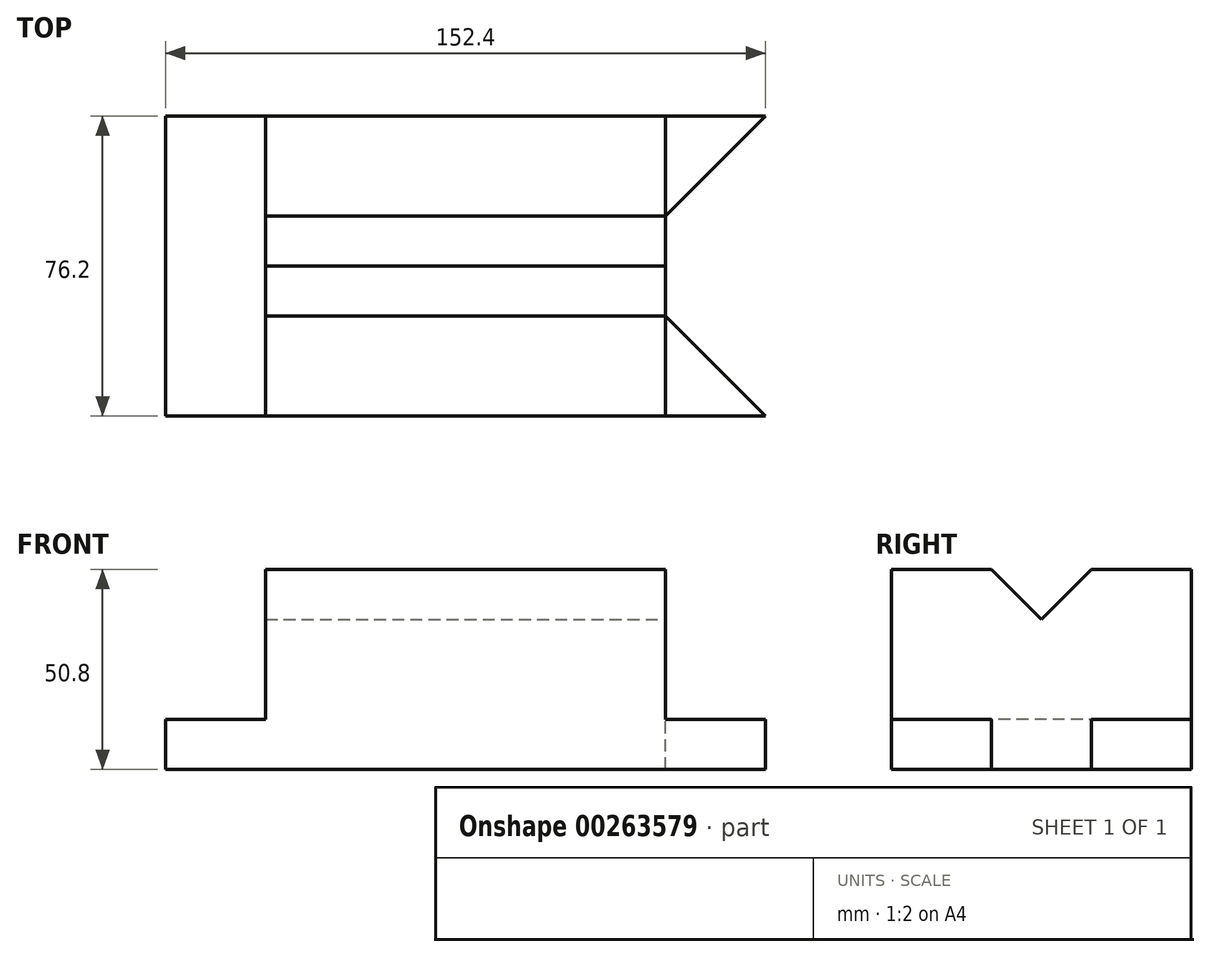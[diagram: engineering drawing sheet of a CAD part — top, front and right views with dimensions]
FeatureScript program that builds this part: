
annotation { "Feature Type Name" : "Feature", "Feature Type Description" : "" }
export const myFeature = defineFeature(function(context is Context, id is Id, definition is map)
    precondition{}
    {
        {
            var Q0;
            Q0=qCreatedBy(makeId("Front.planeOp"),FACE);
            var sketch = newSketch(context, id + "F0", { "sketchPlane" : qUnion([Q0])});
            skLineSegment(sketch, "E0.bottom", {"start": v(-85.05, 48.2) * mm, "end": v(67.35, 48.2) * mm});
            skLineSegment(sketch, "E0.top", {"start": v(-85.05, -2.6) * mm, "end": v(67.35, -2.6) * mm});
            skLineSegment(sketch, "E0.left", {"start": v(-85.05, 48.2) * mm, "end": v(-85.05, -2.6) * mm});
            skLineSegment(sketch, "E0.right", {"start": v(67.35, 48.2) * mm, "end": v(67.35, -2.6) * mm});
            skSolve(sketch);
        }
        {
            var Q0;
            Q0=makeQuery(id+"F0.imprint","IMPRINT",FACE,{"disambiguationData":[TD([[makeQuery(id+"F0.imprint","IMPRINT",EDGE,{"derivedFrom":sQuery(id+"F0.wireOp",EDGE,"E0.bottom")}),-1.0]])]});
            var sketch = newSketch(context, id + "F1", { "sketchPlane" : qUnion([Q0])});
            skSolve(sketch);
        }
        {
            var Q0;
            Q0 = qSketchRegion(id + "F1", true);
            var Q1;
            Q1=makeQuery(id+"F1.imprint","IMPRINT",FACE,{"disambiguationData":[TD([[makeQuery(id+"F1.imprint","IMPRINT",EDGE,{"derivedFrom":makeQuery(id+"F0.imprint","IMPRINT",EDGE,{"derivedFrom":sQuery(id+"F0.wireOp",EDGE,"E0.bottom")})}),-1.0]])]});
            extrude(context, id + "F2", {"entities" : qUnion([Q0, Q1]), "depth" : 76.2 * mm});
        }
        {
            var Q0;
            Q0=makeQuery(id+"F2.opExtrude","CAP_FACE",FACE,{"disambiguationData":[OSD([sQuery(id+"F0.wireOp",EDGE,"E0.bottom"),sQuery(id+"F0.wireOp",EDGE,"E0.top"),sQuery(id+"F0.wireOp",EDGE,"E0.left"),sQuery(id+"F0.wireOp",EDGE,"E0.right")])],"isStart":false});
            var sketch = newSketch(context, id + "F3", { "sketchPlane" : qUnion([Q0])});
            skLineSegment(sketch, "E1", {"start": v(-85.05, 10.1) * mm, "end": v(-59.65, 10.1) * mm});
            skLineSegment(sketch, "E2", {"start": v(-59.65, 10.1) * mm, "end": v(-59.65, 48.2) * mm});
            skLineSegment(sketch, "E3", {"start": v(-59.65, 48.2) * mm, "end": v(-85.05, 48.2) * mm});
            skLineSegment(sketch, "E4", {"start": v(-85.05, 48.2) * mm, "end": v(-85.05, 10.1) * mm});
            skSolve(sketch);
        }
        {
            var Q0;
            Q0=makeQuery(id+"F3.imprint","IMPRINT",FACE,{"disambiguationData":[TD([[makeQuery(id+"F3.imprint","IMPRINT",EDGE,{"derivedFrom":sQuery(id+"F3.wireOp",EDGE,"E1")}),1.0]])]});
            extrude(context, id + "F4", {"entities" : qUnion([Q0]), "operationType" : NewBodyOperationType.REMOVE, "endBound" : BoundingType.THROUGH_ALL, "oppositeDirection" : true, "depth" : 25.4 * mm});
        }
        {
            var Q0;
            Q0=makeQuery(id+"F2.opExtrude","CAP_FACE",FACE,{"disambiguationData":[OSD([sQuery(id+"F0.wireOp",EDGE,"E0.bottom"),sQuery(id+"F0.wireOp",EDGE,"E0.top"),sQuery(id+"F0.wireOp",EDGE,"E0.left"),sQuery(id+"F0.wireOp",EDGE,"E0.right")])],"isStart":false});
            var sketch = newSketch(context, id + "F5", { "sketchPlane" : qUnion([Q0])});
            skLineSegment(sketch, "E5", {"start": v(-85.05, -2.6) * mm, "end": v(-46.95, -2.6) * mm});
            skLineSegment(sketch, "E6", {"start": v(67.35, -2.6) * mm, "end": v(67.35, 10.1) * mm});
            skLineSegment(sketch, "E7", {"start": v(67.35, 10.1) * mm, "end": v(41.95, 10.1) * mm});
            skLineSegment(sketch, "E8", {"start": v(41.95, 10.1) * mm, "end": v(41.95, 48.2) * mm});
            skLineSegment(sketch, "E9", {"start": v(41.95, 48.2) * mm, "end": v(67.35, 48.2) * mm});
            skLineSegment(sketch, "E10", {"start": v(67.35, 48.2) * mm, "end": v(67.35, 10.1) * mm});
            skSolve(sketch);
        }
        {
            var Q0;
            Q0 = qSketchRegion(id + "F5", true);
            extrude(context, id + "F6", {"entities" : qUnion([Q0]), "operationType" : NewBodyOperationType.REMOVE, "endBound" : BoundingType.THROUGH_ALL, "oppositeDirection" : true, "depth" : 25.4 * mm});
        }
        {
            var Q0;
            Q0=makeQuery(id+"F2.opExtrude","SWEPT_FACE",FACE,{"disambiguationData":[OSD([sQuery(id+"F0.wireOp",EDGE,"E0.right")])]});
            var sketch = newSketch(context, id + "F7", { "sketchPlane" : qUnion([Q0])});
            skLineSegment(sketch, "E11", {"start": v(-92.61, 37.64) * mm, "end": v(-76.2, 10.1) * mm});
            skLineSegment(sketch, "E12", {"start": v(-92.61, 37.64) * mm, "end": v(-67.21, 37.64) * mm});
            skLineSegment(sketch, "E13", {"start": v(-67.21, 37.64) * mm, "end": v(0, 10.1) * mm});
            skLineSegment(sketch, "E14", {"start": v(-76.2, 10.1) * mm, "end": v(0, 10.1) * mm});
            skSolve(sketch);
        }
        {
            var Q0;
            Q0=makeQuery(id+"F6.boolean.opBoolean","COPY",FACE,{"derivedFrom":makeQuery(id+"F6.opExtrude","SWEPT_FACE",FACE,{"disambiguationData":[OSD([sQuery(id+"F5.wireOp",EDGE,"E7")])]})});
            var sketch = newSketch(context, id + "F8", { "sketchPlane" : qUnion([Q0])});
            skLineSegment(sketch, "E15", {"start": v(67.35, -76.2) * mm, "end": v(67.35, 0) * mm});
            skLineSegment(sketch, "E16", {"start": v(41.95, -50.8) * mm, "end": v(67.35, -76.2) * mm});
            skLineSegment(sketch, "E17", {"start": v(41.95, -50.8) * mm, "end": v(41.95, -25.4) * mm});
            skLineSegment(sketch, "E18", {"start": v(41.95, -25.4) * mm, "end": v(67.35, 0) * mm});
            skLineSegment(sketch, "E19", {"start": v(67.35, -76.2) * mm, "end": v(78.19, -95.03) * mm});
            skLineSegment(sketch, "E20", {"start": v(78.19, -95.03) * mm, "end": v(78.19, -19.5) * mm});
            skLineSegment(sketch, "E21", {"start": v(78.19, -19.5) * mm, "end": v(67.35, 0) * mm});
            skSolve(sketch);
        }
        {
            var Q0;
            Q0 = qSketchRegion(id + "F8", true);
            extrude(context, id + "F9", {"entities" : qUnion([Q0]), "operationType" : NewBodyOperationType.REMOVE, "endBound" : BoundingType.THROUGH_ALL, "oppositeDirection" : true, "depth" : 25.4 * mm});
        }
        {
            var Q0;
            Q0=makeQuery(id+"F9.boolean.opBoolean","MERGE",FACE,{"derivedFrom":[makeQuery(id+"F6.boolean.opBoolean","COPY",FACE,{"derivedFrom":makeQuery(id+"F6.opExtrude","SWEPT_FACE",FACE,{"disambiguationData":[OSD([sQuery(id+"F5.wireOp",EDGE,"E8")])]})}),makeQuery(id+"F9.opExtrude","SWEPT_FACE",FACE,{"disambiguationData":[OSD([sQuery(id+"F8.wireOp",EDGE,"E17")])]})]});
            var sketch = newSketch(context, id + "F10", { "sketchPlane" : qUnion([Q0])});
            skLineSegment(sketch, "E22", {"start": v(-50.8, 48.2) * mm, "end": v(-38.1, 35.5) * mm});
            skPoint(sketch, "E23.start.orphan", {"position": v(-38.1, 48.2) * mm});
            skLineSegment(sketch, "E24", {"start": v(-38.1, 35.5) * mm, "end": v(-25.4, 48.2) * mm});
            skLineSegment(sketch, "E25", {"start": v(-50.8, 48.2) * mm, "end": v(-25.4, 48.2) * mm});
            skSolve(sketch);
        }
        {
            var Q0;
            Q0 = qSketchRegion(id + "F10", true);
            extrude(context, id + "F11", {"entities" : qUnion([Q0]), "operationType" : NewBodyOperationType.REMOVE, "endBound" : BoundingType.THROUGH_ALL, "oppositeDirection" : true, "depth" : 25.4 * mm});
        }
    });
